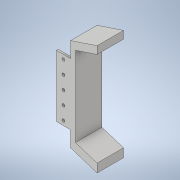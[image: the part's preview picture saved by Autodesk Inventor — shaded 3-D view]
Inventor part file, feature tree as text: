
AUTODESK INVENTOR PART (.ipt)
format: ipt  version: 2020 (Build 240168000, 168)  size: 131,072 bytes
history: native  units: mm
features: sketch x4, extrude x3, other x1, hole x1
ambient origin geometry x8: Origin, YZ Plane, XZ Plane, XY Plane, X Axis, Y Axis, Z Axis, Center Point
bodies: Body1 (feature_tree)
feature tree (9):
  other  "Sólido1"
  extrude  "Extrusión1"  Depth=70.0mm
  extrude  "Extrusión2"  Depth=30.0mm
  extrude  "Extrusión3"  Depth=30.0mm TaperAngle=0.0deg
  hole  "Agujero1"  [1 undecoded]
  sketch  "Boceto1"  dims[d0=16.0mm d1=70.0mm]
  sketch  "Boceto2"  dims[d2=2.0mm d3=0.0mm d4=30.0mm]
  sketch  "Boceto3"  dims[d5=125.0mm d6=30.0mm d7=0.0mm]
  sketch  "Boceto4"  dims[d8=0.0mm d9=0.0mm d10=3.175mm d11=6.0mm d12=4.0mm d13=2.0mm d14=90.0deg d15=8.0mm d16=20.594885mm]
note: 1 required parameter value undecoded (feature->parameter linkage not recoverable at this tier; creation-order binding heuristic only, values carry confidence <= 0.55)
